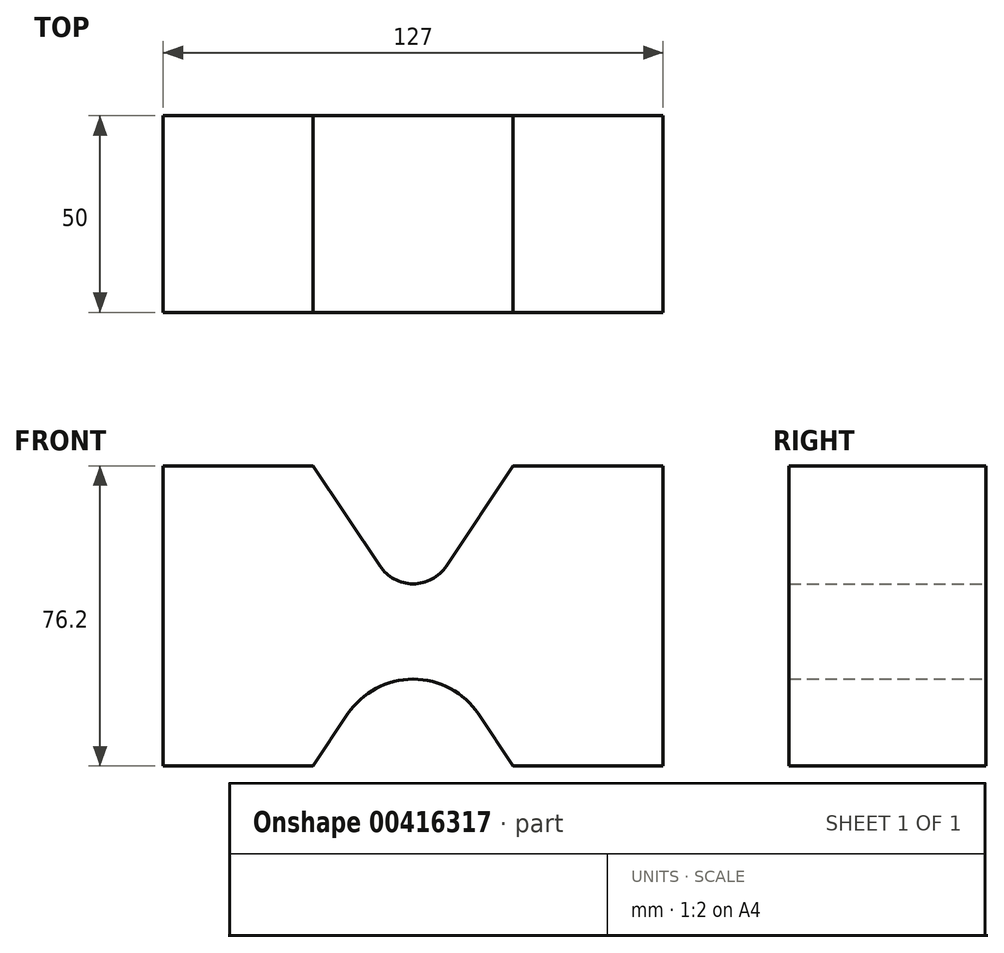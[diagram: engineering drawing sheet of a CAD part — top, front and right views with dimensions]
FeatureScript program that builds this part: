
annotation { "Feature Type Name" : "Feature", "Feature Type Description" : "" }
export const myFeature = defineFeature(function(context is Context, id is Id, definition is map)
    precondition{}
    {
        {
            var Q0;
            Q0=qCreatedBy(makeId("Front.planeOp"),FACE);
            var sketch = newSketch(context, id + "F0", { "sketchPlane" : qUnion([Q0])});
            skLineSegment(sketch, "E0", {"start": v(-63.5, 0) * mm, "end": v(-63.5, 38.1) * mm});
            skLineSegment(sketch, "E1", {"start": v(-63.5, 38.1) * mm, "end": v(-25.4, 38.1) * mm});
            skLineSegment(sketch, "E2", {"start": v(-25.4, 38.1) * mm, "end": v(-8.45, 12.68) * mm});
            skLineSegment(sketch, "E3.MirrorCS", {"start": v(63.5, 38.1) * mm, "end": v(25.4, 38.1) * mm});
            skLineSegment(sketch, "E4.MirrorCS", {"start": v(63.5, 0) * mm, "end": v(63.5, 38.1) * mm});
            skLineSegment(sketch, "E5.MirrorCS", {"start": v(25.4, 38.1) * mm, "end": v(8.45, 12.68) * mm});
            skLineSegment(sketch, "E6.MirrorCS", {"start": v(25.4, -38.1) * mm, "end": v(0, 0) * mm});
            skLineSegment(sketch, "E7.MirrorCS", {"start": v(-63.5, 0) * mm, "end": v(-63.5, -38.1) * mm});
            skLineSegment(sketch, "E8.MirrorCS", {"start": v(-63.5, -38.1) * mm, "end": v(-25.4, -38.1) * mm});
            skLineSegment(sketch, "E9.MirrorCS", {"start": v(63.5, -38.1) * mm, "end": v(25.4, -38.1) * mm});
            skLineSegment(sketch, "E10.MirrorCS", {"start": v(63.5, 0) * mm, "end": v(63.5, -38.1) * mm});
            skLineSegment(sketch, "E11.MirrorCS", {"start": v(-25.4, -38.1) * mm, "end": v(0, 0) * mm});
            skPoint(sketch, "E12.visualSharp", {"position": v(0, 0) * mm});
            skArc(sketch, "E12.filletArc", {"start": v(-8.45, 12.68) * mm, "mid": v(0, 8.16) * mm, "end": v(8.45, 12.68) * mm});
            skSolve(sketch);
        }
        {
            var Q0;
            Q0=makeQuery(id+"F0.imprint","IMPRINT",FACE,{"disambiguationData":[TD([[makeQuery(id+"F0.imprint","IMPRINT",EDGE,{"derivedFrom":sQuery(id+"F0.wireOp",EDGE,"E0")}),-1.0]])]});
            extrude(context, id + "F1", {"entities" : qUnion([Q0]), "depth" : 50 * mm});
        }
        {
            var Q0;
            Q0=makeQuery(id+"F1.opExtrude","SWEPT_EDGE",EDGE,{"disambiguationData":[OSD([sQuery(id+"F0.wireOp",EDGE,"E6.MirrorCS"),sQuery(id+"F0.wireOp",EDGE,"E11.MirrorCS")])]});
            fillet(context, id + "F2", {"entities" : qUnion([Q0]), "radius" : 20 * mm, "tangentPropagation" : true, "allowEdgeOverflow" : false});
        }
    });
